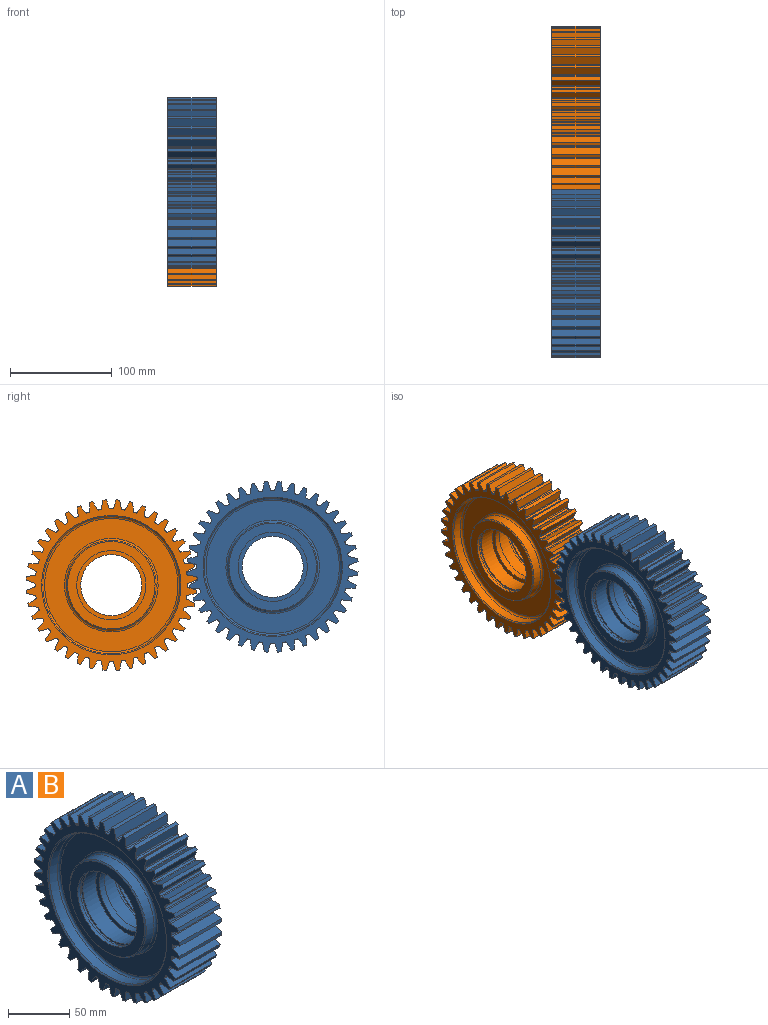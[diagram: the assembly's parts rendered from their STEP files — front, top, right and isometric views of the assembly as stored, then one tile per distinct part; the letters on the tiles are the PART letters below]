
ASSEMBLY  parts=2 mates=1
PART A: 271 faces, bbox 48x167.7x167.7 mm
  f0: cylinder r=84mm len=48mm, axis (-1,0,0), area 155mm2, adj f3,f234,f236,f263
  f1: cylinder r=75mm len=48mm, axis (1,0,0), area 100mm2, adj f2,f5,f234,f236
  f2: cylinder r=1mm len=48mm, axis (1,0,0), area 59.3mm2, adj f1,f3,f234,f236
  f3: plane 48x8.57mm, normal (0,-0.98,0.19), area 418.9mm2, adj f0,f2,f234,f236
  f4: plane 48x7.63mm, normal (0,0.87,0.48), area 418.9mm2, adj f5,f6,f234,f236
  f5: cylinder r=1mm len=48mm, axis (1,0,0), area 59.3mm2, adj f1,f4,f234,f236
  f6: cylinder r=84mm len=48mm, axis (-1,0,0), area 155mm2, adj f4,f9,f234,f236
  f7: cylinder r=75mm len=48mm, axis (1,0,0), area 100mm2, adj f8,f11,f234,f236
  f8: cylinder r=1mm len=48mm, axis (1,0,0), area 59.3mm2, adj f7,f9,f234,f236
  f9: plane 48x8.72mm, normal (0,-1,0.03), area 418.9mm2, adj f6,f8,f234,f236
  f10: plane 48x6.88mm, normal (0,0.79,0.62), area 418.9mm2, adj f11,f12,f234,f236
  f11: cylinder r=1mm len=48mm, axis (1,0,0), area 59.3mm2, adj f7,f10,f234,f236
  f12: cylinder r=84mm len=48mm, axis (-1,0,0), area 155mm2, adj f10,f15,f234,f236
  f13: cylinder r=75mm len=48mm, axis (1,0,0), area 100mm2, adj f14,f17,f234,f236
  f14: cylinder r=1mm len=48mm, axis (1,0,0), area 59.3mm2, adj f13,f15,f234,f236
  f15: plane 48x8.66mm, normal (0,-0.99,-0.12), area 418.9mm2, adj f12,f14,f234,f236
  f16: plane 48x6.38mm, normal (0,0.68,0.73), area 418.9mm2, adj f17,f18,f234,f236
  f17: cylinder r=1mm len=48mm, axis (1,0,0), area 59.3mm2, adj f13,f16,f234,f236
  f18: cylinder r=84mm len=48mm, axis (-1,0,0), area 155mm2, adj f16,f21,f234,f236
  f19: cylinder r=75mm len=48mm, axis (1,0,0), area 100mm2, adj f20,f23,f234,f236
  f20: cylinder r=1mm len=48mm, axis (1,0,0), area 59.3mm2, adj f19,f21,f234,f236
  f21: plane 48x8.39mm, normal (0,-0.96,-0.28), area 418.9mm2, adj f18,f20,f234,f236
  f22: plane 48x7.24mm, normal (0,0.56,0.83), area 418.9mm2, adj f23,f24,f234,f236
  f23: cylinder r=1mm len=48mm, axis (1,0,0), area 59.3mm2, adj f19,f22,f234,f236
  f24: cylinder r=84mm len=48mm, axis (-1,0,0), area 155mm2, adj f22,f27,f234,f236
  f25: cylinder r=75mm len=48mm, axis (1,0,0), area 100mm2, adj f26,f29,f234,f236
  f26: cylinder r=1mm len=48mm, axis (1,0,0), area 59.3mm2, adj f25,f27,f234,f236
  f27: plane 48x7.91mm, normal (0,-0.91,-0.42), area 418.9mm2, adj f24,f26,f234,f236
  f28: plane 48x7.91mm, normal (0,0.42,0.91), area 418.9mm2, adj f29,f30,f234,f236
  f29: cylinder r=1mm len=48mm, axis (1,0,0), area 59.3mm2, adj f25,f28,f234,f236
  f30: cylinder r=84mm len=48mm, axis (-1,0,0), area 155mm2, adj f28,f33,f234,f236
  f31: cylinder r=75mm len=48mm, axis (1,0,0), area 100mm2, adj f32,f35,f234,f236
  f32: cylinder r=1mm len=48mm, axis (1,0,0), area 59.3mm2, adj f31,f33,f234,f236
  f33: plane 48x7.24mm, normal (0,-0.83,-0.56), area 418.9mm2, adj f30,f32,f234,f236
  f34: plane 48x8.39mm, normal (0,0.28,0.96), area 418.9mm2, adj f35,f36,f234,f236
  f35: cylinder r=1mm len=48mm, axis (1,0,0), area 59.3mm2, adj f31,f34,f234,f236
  f36: cylinder r=84mm len=48mm, axis (-1,0,0), area 155mm2, adj f34,f39,f234,f236
  f37: cylinder r=75mm len=48mm, axis (1,0,0), area 100mm2, adj f38,f41,f234,f236
  f38: cylinder r=1mm len=48mm, axis (1,0,0), area 59.3mm2, adj f37,f39,f234,f236
  f39: plane 48x6.38mm, normal (0,-0.73,-0.68), area 418.9mm2, adj f36,f38,f234,f236
  f40: plane 48x8.66mm, normal (0,0.12,0.99), area 418.9mm2, adj f41,f42,f234,f236
  f41: cylinder r=1mm len=48mm, axis (1,0,0), area 59.3mm2, adj f37,f40,f234,f236
  f42: cylinder r=84mm len=48mm, axis (-1,0,0), area 155mm2, adj f40,f45,f234,f236
  f43: cylinder r=75mm len=48mm, axis (1,0,0), area 100mm2, adj f44,f47,f234,f236
  f44: cylinder r=1mm len=48mm, axis (1,0,0), area 59.3mm2, adj f43,f45,f234,f236
  f45: plane 48x6.88mm, normal (0,-0.62,-0.79), area 418.9mm2, adj f42,f44,f234,f236
  f46: plane 48x8.72mm, normal (0,-0.03,1), area 418.9mm2, adj f47,f48,f234,f236
  f47: cylinder r=1mm len=48mm, axis (1,0,0), area 59.3mm2, adj f43,f46,f234,f236
  f48: cylinder r=84mm len=48mm, axis (-1,0,0), area 155mm2, adj f46,f51,f234,f236
  f49: cylinder r=75mm len=48mm, axis (1,0,0), area 100mm2, adj f50,f53,f234,f236
  f50: cylinder r=1mm len=48mm, axis (1,0,0), area 59.3mm2, adj f49,f51,f234,f236
  f51: plane 48x7.63mm, normal (0,-0.48,-0.87), area 418.9mm2, adj f48,f50,f234,f236
  f52: plane 48x8.57mm, normal (0,-0.19,0.98), area 418.9mm2, adj f53,f54,f234,f236
  f53: cylinder r=1mm len=48mm, axis (1,0,0), area 59.3mm2, adj f49,f52,f234,f236
  f54: cylinder r=84mm len=48mm, axis (-1,0,0), area 155mm2, adj f52,f57,f234,f236
  f55: cylinder r=75mm len=48mm, axis (1,0,0), area 100mm2, adj f56,f59,f234,f236
  f56: cylinder r=1mm len=48mm, axis (1,0,0), area 59.3mm2, adj f55,f57,f234,f236
  f57: plane 48x8.2mm, normal (0,-0.34,-0.94), area 418.9mm2, adj f54,f56,f234,f236
  f58: plane 48x8.2mm, normal (0,-0.34,0.94), area 418.9mm2, adj f59,f60,f234,f236
  f59: cylinder r=1mm len=48mm, axis (1,0,0), area 59.3mm2, adj f55,f58,f234,f236
  f60: cylinder r=84mm len=48mm, axis (-1,0,0), area 155mm2, adj f58,f63,f234,f236
  f61: cylinder r=75mm len=48mm, axis (1,0,0), area 100mm2, adj f62,f65,f234,f236
  f62: cylinder r=1mm len=48mm, axis (1,0,0), area 59.3mm2, adj f61,f63,f234,f236
  f63: plane 48x8.57mm, normal (0,-0.19,-0.98), area 418.9mm2, adj f60,f62,f234,f236
  f64: plane 48x7.63mm, normal (0,-0.48,0.87), area 418.9mm2, adj f65,f66,f234,f236
  f65: cylinder r=1mm len=48mm, axis (1,0,0), area 59.3mm2, adj f61,f64,f234,f236
  f66: cylinder r=84mm len=48mm, axis (-1,0,0), area 155mm2, adj f64,f69,f234,f236
  f67: cylinder r=75mm len=48mm, axis (1,0,0), area 100mm2, adj f68,f71,f234,f236
  f68: cylinder r=1mm len=48mm, axis (1,0,0), area 59.3mm2, adj f67,f69,f234,f236
  f69: plane 48x8.72mm, normal (0,-0.03,-1), area 418.9mm2, adj f66,f68,f234,f236
  f70: plane 48x6.88mm, normal (0,-0.62,0.79), area 418.9mm2, adj f71,f72,f234,f236
  f71: cylinder r=1mm len=48mm, axis (1,0,0), area 59.3mm2, adj f67,f70,f234,f236
  f72: cylinder r=84mm len=48mm, axis (-1,0,0), area 155mm2, adj f70,f75,f234,f236
  f73: cylinder r=75mm len=48mm, axis (1,0,0), area 100mm2, adj f74,f77,f234,f236
  f74: cylinder r=1mm len=48mm, axis (1,0,0), area 59.3mm2, adj f73,f75,f234,f236
  f75: plane 48x8.66mm, normal (0,0.12,-0.99), area 418.9mm2, adj f72,f74,f234,f236
  f76: plane 48x6.38mm, normal (0,-0.73,0.68), area 418.9mm2, adj f77,f78,f234,f236
  f77: cylinder r=1mm len=48mm, axis (1,0,0), area 59.3mm2, adj f73,f76,f234,f236
  f78: cylinder r=84mm len=48mm, axis (-1,0,0), area 155mm2, adj f76,f81,f234,f236
  f79: cylinder r=75mm len=48mm, axis (1,0,0), area 100mm2, adj f80,f83,f234,f236
  f80: cylinder r=1mm len=48mm, axis (1,0,0), area 59.3mm2, adj f79,f81,f234,f236
  f81: plane 48x8.39mm, normal (0,0.28,-0.96), area 418.9mm2, adj f78,f80,f234,f236
  f82: plane 48x7.24mm, normal (0,-0.83,0.56), area 418.9mm2, adj f83,f84,f234,f236
  f83: cylinder r=1mm len=48mm, axis (1,0,0), area 59.3mm2, adj f79,f82,f234,f236
  f84: cylinder r=84mm len=48mm, axis (-1,0,0), area 155mm2, adj f82,f87,f234,f236
  f85: cylinder r=75mm len=48mm, axis (1,0,0), area 100mm2, adj f86,f89,f234,f236
  f86: cylinder r=1mm len=48mm, axis (1,0,0), area 59.3mm2, adj f85,f87,f234,f236
  f87: plane 48x7.91mm, normal (0,0.42,-0.91), area 418.9mm2, adj f84,f86,f234,f236
  f88: plane 48x7.91mm, normal (0,-0.91,0.42), area 418.9mm2, adj f89,f90,f234,f236
  f89: cylinder r=1mm len=48mm, axis (1,0,0), area 59.3mm2, adj f85,f88,f234,f236
  f90: cylinder r=84mm len=48mm, axis (-1,0,0), area 155mm2, adj f88,f93,f234,f236
  f91: cylinder r=75mm len=48mm, axis (1,0,0), area 100mm2, adj f92,f95,f234,f236
  f92: cylinder r=1mm len=48mm, axis (1,0,0), area 59.3mm2, adj f91,f93,f234,f236
  f93: plane 48x7.24mm, normal (0,0.56,-0.83), area 418.9mm2, adj f90,f92,f234,f236
  f94: plane 48x8.39mm, normal (0,-0.96,0.28), area 418.9mm2, adj f95,f96,f234,f236
  f95: cylinder r=1mm len=48mm, axis (1,0,0), area 59.3mm2, adj f91,f94,f234,f236
  f96: cylinder r=84mm len=48mm, axis (-1,0,0), area 155mm2, adj f94,f99,f234,f236
  f97: cylinder r=75mm len=48mm, axis (1,0,0), area 100mm2, adj f98,f101,f234,f236
  f98: cylinder r=1mm len=48mm, axis (1,0,0), area 59.3mm2, adj f97,f99,f234,f236
  f99: plane 48x6.38mm, normal (0,0.68,-0.73), area 418.9mm2, adj f96,f98,f234,f236
  f100: plane 48x8.66mm, normal (0,-0.99,0.12), area 418.9mm2, adj f101,f102,f234,f236
  f101: cylinder r=1mm len=48mm, axis (1,0,0), area 59.3mm2, adj f97,f100,f234,f236
  f102: cylinder r=84mm len=48mm, axis (-1,0,0), area 155mm2, adj f100,f105,f234,f236
  f103: cylinder r=75mm len=48mm, axis (1,0,0), area 100mm2, adj f104,f107,f234,f236
  f104: cylinder r=1mm len=48mm, axis (1,0,0), area 59.3mm2, adj f103,f105,f234,f236
  f105: plane 48x6.88mm, normal (0,0.79,-0.62), area 418.9mm2, adj f102,f104,f234,f236
  f106: plane 48x8.72mm, normal (0,-1,-0.03), area 418.9mm2, adj f107,f108,f234,f236
  f107: cylinder r=1mm len=48mm, axis (1,0,0), area 59.3mm2, adj f103,f106,f234,f236
  f108: cylinder r=84mm len=48mm, axis (-1,0,0), area 155mm2, adj f106,f111,f234,f236
  f109: cylinder r=75mm len=48mm, axis (1,0,0), area 100mm2, adj f110,f113,f234,f236
  f110: cylinder r=1mm len=48mm, axis (1,0,0), area 59.3mm2, adj f109,f111,f234,f236
  f111: plane 48x7.63mm, normal (0,0.87,-0.48), area 418.9mm2, adj f108,f110,f234,f236
  f112: plane 48x8.57mm, normal (0,-0.98,-0.19), area 418.9mm2, adj f113,f114,f234,f236
  f113: cylinder r=1mm len=48mm, axis (1,0,0), area 59.3mm2, adj f109,f112,f234,f236
  f114: cylinder r=84mm len=48mm, axis (-1,0,0), area 155mm2, adj f112,f117,f234,f236
  f115: cylinder r=75mm len=48mm, axis (1,0,0), area 100mm2, adj f116,f119,f234,f236
  f116: cylinder r=1mm len=48mm, axis (1,0,0), area 59.3mm2, adj f115,f117,f234,f236
  f117: plane 48x8.2mm, normal (0,0.94,-0.34), area 418.9mm2, adj f114,f116,f234,f236
  f118: plane 48x8.2mm, normal (0,-0.94,-0.34), area 418.9mm2, adj f119,f120,f234,f236
  f119: cylinder r=1mm len=48mm, axis (1,0,0), area 59.3mm2, adj f115,f118,f234,f236
  f120: cylinder r=84mm len=48mm, axis (-1,0,0), area 155mm2, adj f118,f123,f234,f236
  f121: cylinder r=75mm len=48mm, axis (1,0,0), area 100mm2, adj f122,f125,f234,f236
  f122: cylinder r=1mm len=48mm, axis (1,0,0), area 59.3mm2, adj f121,f123,f234,f236
  f123: plane 48x8.57mm, normal (0,0.98,-0.19), area 418.9mm2, adj f120,f122,f234,f236
  f124: plane 48x7.63mm, normal (0,-0.87,-0.48), area 418.9mm2, adj f125,f126,f234,f236
  f125: cylinder r=1mm len=48mm, axis (1,0,0), area 59.3mm2, adj f121,f124,f234,f236
  f126: cylinder r=84mm len=48mm, axis (-1,0,0), area 155mm2, adj f124,f129,f234,f236
  f127: cylinder r=75mm len=48mm, axis (1,0,0), area 100mm2, adj f128,f131,f234,f236
  f128: cylinder r=1mm len=48mm, axis (1,0,0), area 59.3mm2, adj f127,f129,f234,f236
  f129: plane 48x8.72mm, normal (0,1,-0.03), area 418.9mm2, adj f126,f128,f234,f236
  f130: plane 48x6.88mm, normal (0,-0.79,-0.62), area 418.9mm2, adj f131,f132,f234,f236
  f131: cylinder r=1mm len=48mm, axis (1,0,0), area 59.3mm2, adj f127,f130,f234,f236
  f132: cylinder r=84mm len=48mm, axis (-1,0,0), area 155mm2, adj f130,f135,f234,f236
  f133: cylinder r=75mm len=48mm, axis (1,0,0), area 100mm2, adj f134,f137,f234,f236
  f134: cylinder r=1mm len=48mm, axis (1,0,0), area 59.3mm2, adj f133,f135,f234,f236
  f135: plane 48x8.66mm, normal (0,0.99,0.12), area 418.9mm2, adj f132,f134,f234,f236
  f136: plane 48x6.38mm, normal (0,-0.68,-0.73), area 418.9mm2, adj f137,f138,f234,f236
  f137: cylinder r=1mm len=48mm, axis (1,0,0), area 59.3mm2, adj f133,f136,f234,f236
  f138: cylinder r=84mm len=48mm, axis (-1,0,0), area 155mm2, adj f136,f141,f234,f236
  f139: cylinder r=75mm len=48mm, axis (1,0,0), area 100mm2, adj f140,f143,f234,f236
  f140: cylinder r=1mm len=48mm, axis (1,0,0), area 59.3mm2, adj f139,f141,f234,f236
  f141: plane 48x8.39mm, normal (0,0.96,0.28), area 418.9mm2, adj f138,f140,f234,f236
  f142: plane 48x7.24mm, normal (0,-0.56,-0.83), area 418.9mm2, adj f143,f144,f234,f236
  f143: cylinder r=1mm len=48mm, axis (1,0,0), area 59.3mm2, adj f139,f142,f234,f236
  f144: cylinder r=84mm len=48mm, axis (-1,0,0), area 155mm2, adj f142,f147,f234,f236
  f145: cylinder r=75mm len=48mm, axis (1,0,0), area 100mm2, adj f146,f149,f234,f236
  f146: cylinder r=1mm len=48mm, axis (1,0,0), area 59.3mm2, adj f145,f147,f234,f236
  f147: plane 48x7.91mm, normal (0,0.91,0.42), area 418.9mm2, adj f144,f146,f234,f236
  f148: plane 48x7.91mm, normal (0,-0.42,-0.91), area 418.9mm2, adj f149,f150,f234,f236
  f149: cylinder r=1mm len=48mm, axis (1,0,0), area 59.3mm2, adj f145,f148,f234,f236
  f150: cylinder r=84mm len=48mm, axis (-1,0,0), area 155mm2, adj f148,f153,f234,f236
  f151: cylinder r=75mm len=48mm, axis (1,0,0), area 100mm2, adj f152,f155,f234,f236
  f152: cylinder r=1mm len=48mm, axis (1,0,0), area 59.3mm2, adj f151,f153,f234,f236
  f153: plane 48x7.24mm, normal (0,0.83,0.56), area 418.9mm2, adj f150,f152,f234,f236
  f154: plane 48x8.39mm, normal (0,-0.28,-0.96), area 418.9mm2, adj f155,f156,f234,f236
  f155: cylinder r=1mm len=48mm, axis (1,0,0), area 59.3mm2, adj f151,f154,f234,f236
  f156: cylinder r=84mm len=48mm, axis (-1,0,0), area 155mm2, adj f154,f159,f234,f236
  f157: cylinder r=75mm len=48mm, axis (1,0,0), area 100mm2, adj f158,f161,f234,f236
  f158: cylinder r=1mm len=48mm, axis (1,0,0), area 59.3mm2, adj f157,f159,f234,f236
  f159: plane 48x6.38mm, normal (0,0.73,0.68), area 418.9mm2, adj f156,f158,f234,f236
  f160: plane 48x8.66mm, normal (0,-0.12,-0.99), area 418.9mm2, adj f161,f162,f234,f236
  f161: cylinder r=1mm len=48mm, axis (1,0,0), area 59.3mm2, adj f157,f160,f234,f236
  f162: cylinder r=84mm len=48mm, axis (-1,0,0), area 155mm2, adj f160,f165,f234,f236
  f163: cylinder r=75mm len=48mm, axis (1,0,0), area 100mm2, adj f164,f167,f234,f236
  f164: cylinder r=1mm len=48mm, axis (1,0,0), area 59.3mm2, adj f163,f165,f234,f236
  f165: plane 48x6.88mm, normal (0,0.62,0.79), area 418.9mm2, adj f162,f164,f234,f236
  f166: plane 48x8.72mm, normal (0,0.03,-1), area 418.9mm2, adj f167,f168,f234,f236
  f167: cylinder r=1mm len=48mm, axis (1,0,0), area 59.3mm2, adj f163,f166,f234,f236
  f168: cylinder r=84mm len=48mm, axis (-1,0,0), area 155mm2, adj f166,f171,f234,f236
  f169: cylinder r=75mm len=48mm, axis (1,0,0), area 100mm2, adj f170,f173,f234,f236
  f170: cylinder r=1mm len=48mm, axis (1,0,0), area 59.3mm2, adj f169,f171,f234,f236
  f171: plane 48x7.63mm, normal (0,0.48,0.87), area 418.9mm2, adj f168,f170,f234,f236
  f172: plane 48x8.57mm, normal (0,0.19,-0.98), area 418.9mm2, adj f173,f174,f234,f236
  f173: cylinder r=1mm len=48mm, axis (1,0,0), area 59.3mm2, adj f169,f172,f234,f236
  f174: cylinder r=84mm len=48mm, axis (-1,0,0), area 155mm2, adj f172,f177,f234,f236
  f175: cylinder r=75mm len=48mm, axis (1,0,0), area 100mm2, adj f176,f179,f234,f236
  f176: cylinder r=1mm len=48mm, axis (1,0,0), area 59.3mm2, adj f175,f177,f234,f236
  f177: plane 48x8.2mm, normal (0,0.34,0.94), area 418.9mm2, adj f174,f176,f234,f236
  f178: plane 48x8.2mm, normal (0,0.34,-0.94), area 418.9mm2, adj f179,f180,f234,f236
  f179: cylinder r=1mm len=48mm, axis (1,0,0), area 59.3mm2, adj f175,f178,f234,f236
  f180: cylinder r=84mm len=48mm, axis (-1,0,0), area 155mm2, adj f178,f183,f234,f236
  f181: cylinder r=75mm len=48mm, axis (1,0,0), area 100mm2, adj f182,f185,f234,f236
  f182: cylinder r=1mm len=48mm, axis (1,0,0), area 59.3mm2, adj f181,f183,f234,f236
  f183: plane 48x8.57mm, normal (0,0.19,0.98), area 418.9mm2, adj f180,f182,f234,f236
  f184: plane 48x7.63mm, normal (0,0.48,-0.87), area 418.9mm2, adj f185,f186,f234,f236
  f185: cylinder r=1mm len=48mm, axis (1,0,0), area 59.3mm2, adj f181,f184,f234,f236
  f186: cylinder r=84mm len=48mm, axis (-1,0,0), area 155mm2, adj f184,f189,f234,f236
  f187: cylinder r=75mm len=48mm, axis (1,0,0), area 100mm2, adj f188,f191,f234,f236
  f188: cylinder r=1mm len=48mm, axis (1,0,0), area 59.3mm2, adj f187,f189,f234,f236
  f189: plane 48x8.72mm, normal (0,0.03,1), area 418.9mm2, adj f186,f188,f234,f236
  f190: plane 48x6.88mm, normal (0,0.62,-0.79), area 418.9mm2, adj f191,f192,f234,f236
  f191: cylinder r=1mm len=48mm, axis (1,0,0), area 59.3mm2, adj f187,f190,f234,f236
  f192: cylinder r=84mm len=48mm, axis (-1,0,0), area 155mm2, adj f190,f195,f234,f236
  f193: cylinder r=75mm len=48mm, axis (1,0,0), area 100mm2, adj f194,f197,f234,f236
  f194: cylinder r=1mm len=48mm, axis (1,0,0), area 59.3mm2, adj f193,f195,f234,f236
  f195: plane 48x8.66mm, normal (0,-0.12,0.99), area 418.9mm2, adj f192,f194,f234,f236
  f196: plane 48x6.38mm, normal (0,0.73,-0.68), area 418.9mm2, adj f197,f198,f234,f236
  f197: cylinder r=1mm len=48mm, axis (1,0,0), area 59.3mm2, adj f193,f196,f234,f236
  f198: cylinder r=84mm len=48mm, axis (-1,0,0), area 155mm2, adj f196,f201,f234,f236
  f199: cylinder r=75mm len=48mm, axis (1,0,0), area 100mm2, adj f200,f203,f234,f236
  f200: cylinder r=1mm len=48mm, axis (1,0,0), area 59.3mm2, adj f199,f201,f234,f236
  f201: plane 48x8.39mm, normal (0,-0.28,0.96), area 418.9mm2, adj f198,f200,f234,f236
  f202: plane 48x7.24mm, normal (0,0.83,-0.56), area 418.9mm2, adj f203,f204,f234,f236
  f203: cylinder r=1mm len=48mm, axis (1,0,0), area 59.3mm2, adj f199,f202,f234,f236
  f204: cylinder r=84mm len=48mm, axis (-1,0,0), area 155mm2, adj f202,f207,f234,f236
  f205: cylinder r=75mm len=48mm, axis (1,0,0), area 100mm2, adj f206,f209,f234,f236
  f206: cylinder r=1mm len=48mm, axis (1,0,0), area 59.3mm2, adj f205,f207,f234,f236
  f207: plane 48x7.91mm, normal (0,-0.42,0.91), area 418.9mm2, adj f204,f206,f234,f236
  f208: plane 48x7.91mm, normal (0,0.91,-0.42), area 418.9mm2, adj f209,f210,f234,f236
  f209: cylinder r=1mm len=48mm, axis (1,0,0), area 59.3mm2, adj f205,f208,f234,f236
  f210: cylinder r=84mm len=48mm, axis (-1,0,0), area 155mm2, adj f208,f213,f234,f236
  f211: cylinder r=75mm len=48mm, axis (1,0,0), area 100mm2, adj f212,f215,f234,f236
  f212: cylinder r=1mm len=48mm, axis (1,0,0), area 59.3mm2, adj f211,f213,f234,f236
  f213: plane 48x7.24mm, normal (0,-0.56,0.83), area 418.9mm2, adj f210,f212,f234,f236
  f214: plane 48x8.39mm, normal (0,0.96,-0.28), area 418.9mm2, adj f215,f216,f234,f236
  f215: cylinder r=1mm len=48mm, axis (1,0,0), area 59.3mm2, adj f211,f214,f234,f236
  f216: cylinder r=84mm len=48mm, axis (-1,0,0), area 155mm2, adj f214,f219,f234,f236
  f217: cylinder r=75mm len=48mm, axis (1,0,0), area 100mm2, adj f218,f221,f234,f236
  f218: cylinder r=1mm len=48mm, axis (1,0,0), area 59.3mm2, adj f217,f219,f234,f236
  f219: plane 48x6.38mm, normal (0,-0.68,0.73), area 418.9mm2, adj f216,f218,f234,f236
  f220: plane 48x8.66mm, normal (0,0.99,-0.12), area 418.9mm2, adj f221,f222,f234,f236
  f221: cylinder r=1mm len=48mm, axis (1,0,0), area 59.3mm2, adj f217,f220,f234,f236
  f222: cylinder r=84mm len=48mm, axis (-1,0,0), area 155mm2, adj f220,f225,f234,f236
  f223: cylinder r=75mm len=48mm, axis (1,0,0), area 100mm2, adj f224,f227,f234,f236
  f224: cylinder r=1mm len=48mm, axis (1,0,0), area 59.3mm2, adj f223,f225,f234,f236
  f225: plane 48x6.88mm, normal (0,-0.79,0.62), area 418.9mm2, adj f222,f224,f234,f236
  f226: plane 48x8.72mm, normal (0,1,0.03), area 418.9mm2, adj f227,f228,f234,f236
  f227: cylinder r=1mm len=48mm, axis (1,0,0), area 59.3mm2, adj f223,f226,f234,f236
  f228: cylinder r=84mm len=48mm, axis (-1,0,0), area 155mm2, adj f226,f231,f234,f236
  f229: cylinder r=75mm len=48mm, axis (1,0,0), area 100mm2, adj f230,f233,f234,f236
  f230: cylinder r=1mm len=48mm, axis (1,0,0), area 59.3mm2, adj f229,f231,f234,f236
  f231: plane 48x7.63mm, normal (0,-0.87,0.48), area 418.9mm2, adj f228,f230,f234,f236
  f232: plane 48x8.57mm, normal (0,0.98,0.19), area 418.9mm2, adj f233,f234,f235,f236
  f233: cylinder r=1mm len=48mm, axis (1,0,0), area 59.3mm2, adj f229,f232,f234,f236
  f234: plane 167.7x167.7mm, normal (1,0,0), area 5007.3mm2, adj f0,f1,f2,f3,f4,f5,f6,f7
  f235: cylinder r=84mm len=48mm, axis (-1,0,0), area 155mm2, adj f232,f234,f236,f264
  f236: plane 167.7x167.7mm, normal (-1,0,0), area 5007.3mm2, adj f0,f1,f2,f3,f4,f5,f6,f7
  f237: plane 131x131mm, normal (-1,0,0), area 6830.6mm2, adj f238,f261
  f238: torus R=46mm, axis (-1,0,0), area 882.9mm2, adj f237,f239
  f239: cylinder r=44mm len=88mm, axis (-1,0,0), area 2488.1mm2, adj f238,f267
  f240: plane 86x86mm, normal (-1,0,0), area 2177.1mm2, adj f241,f267
  f241: cylinder r=34mm len=68mm, axis (-1,0,0), area 640.9mm2, adj f240,f242
  f242: plane 71x71mm, normal (1,0,0), area 327.5mm2, adj f241,f243
  f243: cylinder r=35.5mm len=71mm, axis (-1,0,0), area 669.2mm2, adj f242,f244
  f244: plane 71x71mm, normal (-1,0,0), area 327.5mm2, adj f243,f245
  f245: cylinder r=34mm len=68mm, axis (-1,0,0), area 3204.4mm2, adj f244,f246
  f246: plane 68x68mm, normal (-1,0,0), area 804.2mm2, adj f245,f247
  f247: cylinder r=30mm len=60mm, axis (-1,0,0), area 1131mm2, adj f246,f248
  f248: plane 68x68mm, normal (1,0,0), area 804.2mm2, adj f247,f249
  f249: cylinder r=34mm len=68mm, axis (-1,0,0), area 3204.4mm2, adj f248,f250
  f250: plane 71x71mm, normal (1,0,0), area 327.5mm2, adj f249,f251
  f251: cylinder r=35.5mm len=71mm, axis (-1,0,0), area 669.2mm2, adj f250,f252
  f252: plane 71x71mm, normal (-1,0,0), area 327.5mm2, adj f251,f253
  f253: cylinder r=34mm len=68mm, axis (-1,0,0), area 640.9mm2, adj f252,f254
  f254: plane 86x86mm, normal (1,0,0), area 2177.1mm2, adj f253,f269
  f255: cylinder r=44mm len=88mm, axis (-1,0,0), area 2488.1mm2, adj f256,f269
  f256: torus R=46mm, axis (-1,0,0), area 882.9mm2, adj f255,f257
  f257: plane 131x131mm, normal (1,0,0), area 6830.6mm2, adj f256,f258
  f258: torus R=65.5mm, axis (-1,0,0), area 1318.1mm2, adj f257,f259
  f259: cylinder r=67.5mm len=135mm, axis (-1,0,0), area 3817mm2, adj f258,f270
  f260: cylinder r=67.5mm len=135mm, axis (-1,0,0), area 3817mm2, adj f261,f268
  f261: torus R=65.5mm, axis (-1,0,0), area 1318.1mm2, adj f237,f260
  f262: cylinder r=1mm len=48mm, axis (1,0,0), area 59.3mm2, adj f234,f236,f263,f266
  f263: plane 48x8.2mm, normal (0,0.94,0.34), area 418.9mm2, adj f0,f234,f236,f262
  f264: plane 48x8.2mm, normal (0,-0.94,0.34), area 418.9mm2, adj f234,f235,f236,f265
  f265: cylinder r=1mm len=48mm, axis (1,0,0), area 59.3mm2, adj f234,f236,f264,f266
  f266: cylinder r=75mm len=48mm, axis (1,0,0), area 100mm2, adj f234,f236,f262,f265
  f267: cone r=43mm half-angle=45deg, axis (1,0,0), area 386.5mm2, adj f239,f240
  f268: cone r=67.5mm half-angle=45deg, axis (-1,0,0), area 604.2mm2, adj f236,f260
  f269: cone r=44mm half-angle=45deg, axis (-1,0,0), area 386.5mm2, adj f254,f255
  f270: cone r=68.5mm half-angle=45deg, axis (1,0,0), area 604.2mm2, adj f234,f259
PART B: same geometry as A
PLACE A rot(axis=(1,0,0),135deg) t=(1.8,-158.01,17.37)mm
PLACE B t=(1.8,0.63,-0.69)mm fixed
MATE fastened B.f52 <-> A.f82  axis (0,-0.19,0.98) through (1.8,-78.69,8.34)mm
